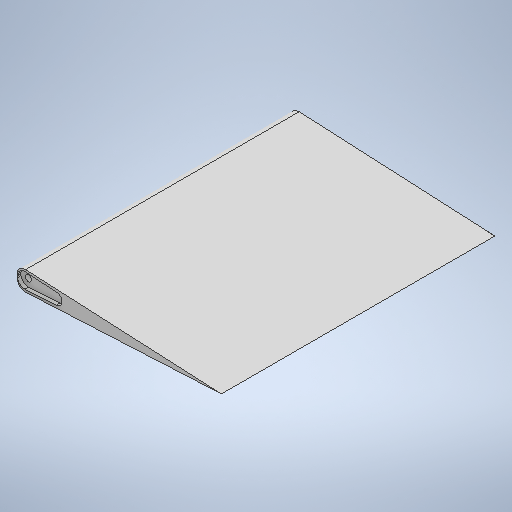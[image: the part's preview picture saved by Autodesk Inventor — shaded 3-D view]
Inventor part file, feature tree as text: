
AUTODESK INVENTOR PART (.ipt)
format: ipt  version: 2025.2 (Build 292293000, 293)  size: 228,864 bytes
history: native  units: in
note: dims shown in document units (in); Inventor stores cm internally (conversion verified against a paired STEP export)
features: extrude x3, sketch x3, projected_geometry x1
ambient origin geometry x8: Origin, YZ Plane, XZ Plane, XY Plane, X Axis, Y Axis, Z Axis, Center Point
bodies: Solid1 (feature_tree)
feature tree (7):
  extrude  "Extrusion1"  Depth=0.5in
  extrude  "Extrusion2"  Depth=6.693in TaperAngle=0.0deg
  extrude  "Extrusion3"  Depth=0.0886in
  sketch  "Sketch1"  dims[d0=5.0in d1=0.5in]
  sketch  "Sketch2"  dims[d2=0.2in d3=6.693in d4=0.0in]
  sketch  "Sketch3"  dims[d5=0.0886in d6=0.0in d7=0.15in d8=6.7in d9=0.0in]
  projected_geometry  "Projected Loop1"
